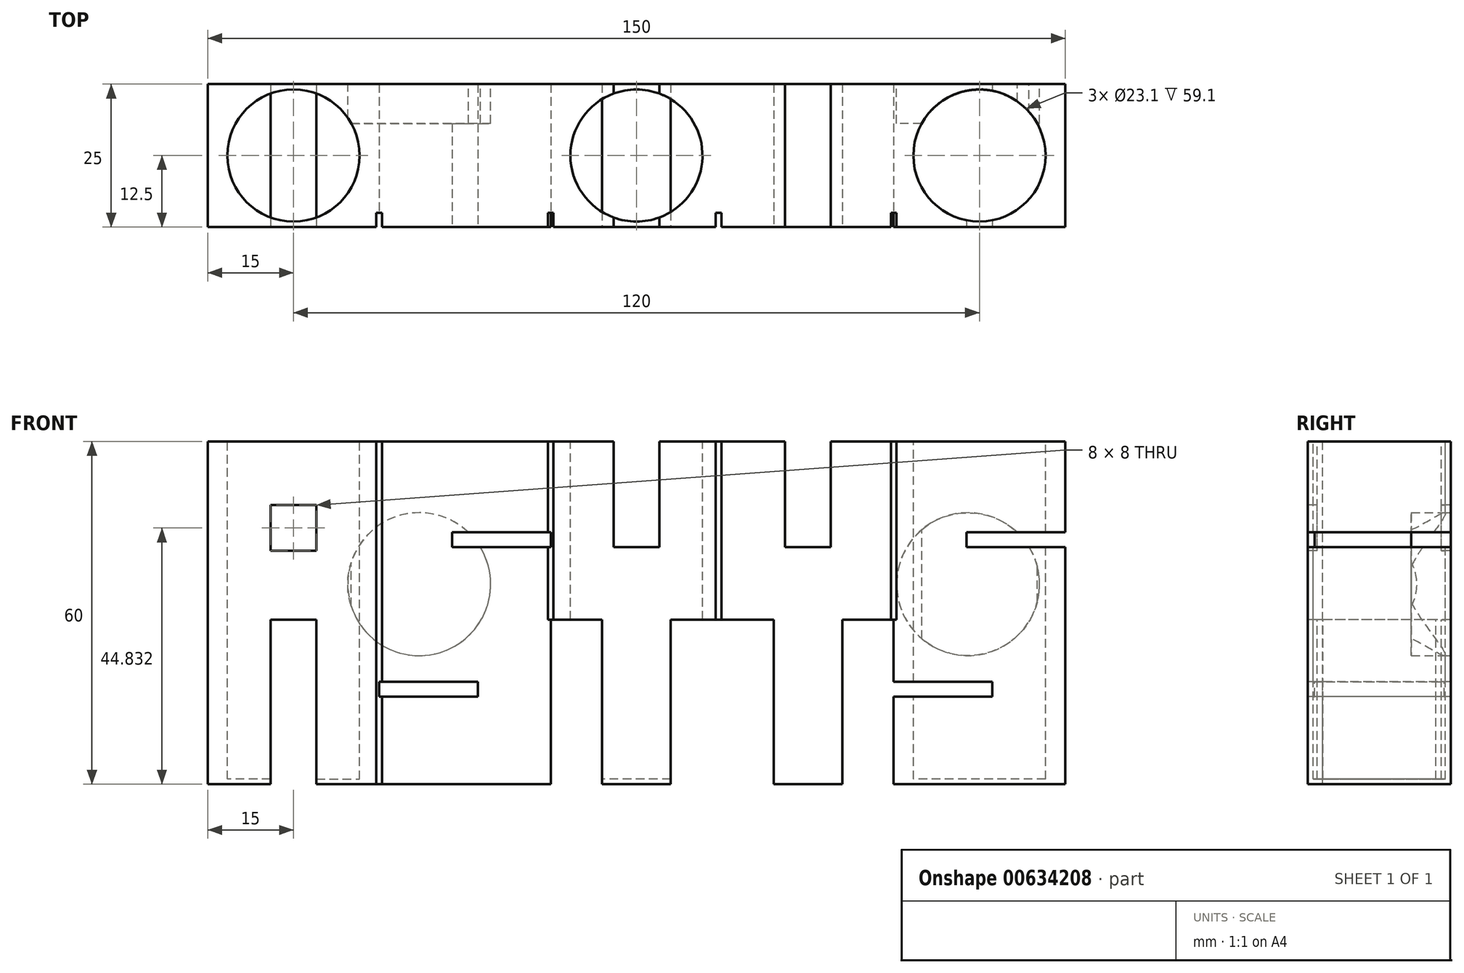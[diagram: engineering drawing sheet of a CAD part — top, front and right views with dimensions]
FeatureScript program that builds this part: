
annotation { "Feature Type Name" : "Feature", "Feature Type Description" : "" }
export const myFeature = defineFeature(function(context is Context, id is Id, definition is map)
    precondition{}
    {
        {
            var Q0;
            Q0=qCreatedBy(makeId("Front.planeOp"),FACE);
            var sketch = newSketch(context, id + "F0", { "sketchPlane" : qUnion([Q0])});
            skLineSegment(sketch, "E0.bottom", {"start": v(-75, 38.6) * mm, "end": v(75, 38.6) * mm});
            skLineSegment(sketch, "E0.top", {"start": v(-75, -21.4) * mm, "end": v(75, -21.4) * mm});
            skLineSegment(sketch, "E0.left", {"start": v(-75, 38.6) * mm, "end": v(-75, -21.4) * mm});
            skLineSegment(sketch, "E0.right", {"start": v(75, 38.6) * mm, "end": v(75, -21.4) * mm});
            skSolve(sketch);
        }
        {
            var Q0;
            Q0 = qSketchRegion(id + "F0", true);
            extrude(context, id + "F1", {"entities" : qUnion([Q0]), "depth" : 25 * mm, "offsetDistance" : 25 * mm});
        }
        {
            var Q0;
            Q0=makeQuery(id+"F1.opExtrude","SWEPT_FACE",FACE,{"disambiguationData":[OSD([sQuery(id+"F0.wireOp",EDGE,"E0.bottom")])]});
            var sketch = newSketch(context, id + "F2", { "sketchPlane" : qUnion([Q0])});
            skLineSegment(sketch, "E1.bottom", {"start": v(-73, -2) * mm, "end": v(73, -2) * mm});
            skLineSegment(sketch, "E1.top", {"start": v(-73, -23) * mm, "end": v(73, -23) * mm});
            skLineSegment(sketch, "E1.left", {"start": v(-73, -2) * mm, "end": v(-73, -23) * mm});
            skLineSegment(sketch, "E1.right", {"start": v(73, -2) * mm, "end": v(73, -23) * mm});
            skLineSegment(sketch, "E2.MirrorCS", {"start": v(219, -2) * mm, "end": v(219, -23) * mm});
            skSolve(sketch);
        }
        {
            var Q0;
            Q0 = qSketchRegion(id + "F2", true);
            extrude(context, id + "F3", {"entities" : qUnion([Q0]), "operationType" : NewBodyOperationType.ADD, "oppositeDirection" : true, "depth" : 2 * mm, "offsetDistance" : 25 * mm});
        }
        {
            var Q0;
            Q0=makeQuery(id+"F3.boolean.opBoolean","MERGE",FACE,{"derivedFrom":[makeQuery(id+"F1.opExtrude","SWEPT_FACE",FACE,{"disambiguationData":[OSD([sQuery(id+"F0.wireOp",EDGE,"E0.bottom")])]}),makeQuery(id+"F3.opExtrude","CAP_FACE",FACE,{"disambiguationData":[OSD([sQuery(id+"F2.wireOp",EDGE,"E1.bottom"),sQuery(id+"F2.wireOp",EDGE,"E1.top"),sQuery(id+"F2.wireOp",EDGE,"E1.left"),sQuery(id+"F2.wireOp",EDGE,"E1.right")])],"isStart":true})]});
            var sketch = newSketch(context, id + "F4", { "sketchPlane" : qUnion([Q0])});
            skCircle(sketch, "E3", {"center": v(60, -12.5) * mm, "radius": 11.55 * mm});
            skCircle(sketch, "E4.MirrorC", {"center": v(-60, -12.5) * mm, "radius": 11.55 * mm});
            skCircle(sketch, "E5", {"center": v(0, -12.5) * mm, "radius": 11.55 * mm});
            skSolve(sketch);
        }
        {
            var Q0;
            Q0 = qSketchRegion(id + "F4", true);
            extrude(context, id + "F5", {"entities" : qUnion([Q0]), "operationType" : NewBodyOperationType.REMOVE, "oppositeDirection" : true, "depth" : 59.1 * mm, "offsetDistance" : 25 * mm});
        }
        {
            var Q0;
            Q0=makeQuery(id+"F1.opExtrude","CAP_FACE",FACE,{"disambiguationData":[OSD([sQuery(id+"F0.wireOp",EDGE,"E0.bottom"),sQuery(id+"F0.wireOp",EDGE,"E0.top"),sQuery(id+"F0.wireOp",EDGE,"E0.left"),sQuery(id+"F0.wireOp",EDGE,"E0.right")])],"isStart":true});
            var sketch = newSketch(context, id + "F6", { "sketchPlane" : qUnion([Q0])});
            skCircle(sketch, "E6", {"center": v(-58, 13.6) * mm, "radius": 12.5 * mm});
            skCircle(sketch, "E7.MirrorC", {"center": v(38, 13.6) * mm, "radius": 12.5 * mm});
            skSolve(sketch);
        }
        {
            var Q0;
            Q0 = qSketchRegion(id + "F6", true);
            extrude(context, id + "F7", {"entities" : qUnion([Q0]), "operationType" : NewBodyOperationType.REMOVE, "oppositeDirection" : true, "depth" : 6.9 * mm, "offsetDistance" : 25 * mm});
        }
        {
            var Q0;
            Q0=makeQuery(id+"F1.opExtrude","CAP_FACE",FACE,{"disambiguationData":[OSD([sQuery(id+"F0.wireOp",EDGE,"E0.bottom"),sQuery(id+"F0.wireOp",EDGE,"E0.top"),sQuery(id+"F0.wireOp",EDGE,"E0.left"),sQuery(id+"F0.wireOp",EDGE,"E0.right")])],"isStart":false});
            var sketch = newSketch(context, id + "F8", { "sketchPlane" : qUnion([Q0])});
            skLineSegment(sketch, "E8.bottom", {"start": v(-75, 38.6) * mm, "end": v(-45, 38.6) * mm});
            skLineSegment(sketch, "E8.top", {"start": v(-75, -21.4) * mm, "end": v(-45, -21.4) * mm});
            skLineSegment(sketch, "E8.left", {"start": v(-75, 38.6) * mm, "end": v(-75, -21.4) * mm});
            skLineSegment(sketch, "E8.right", {"start": v(-45, 38.6) * mm, "end": v(-45, -21.4) * mm});
            skLineSegment(sketch, "E9", {"start": v(-60, 38.6) * mm, "end": v(-60, -21.4) * mm});
            skLineSegment(sketch, "E10", {"start": v(-64, -21.4) * mm, "end": v(-64, 7.4) * mm});
            skLineSegment(sketch, "E11", {"start": v(-64, 7.4) * mm, "end": v(-60, 7.4) * mm});
            skLineSegment(sketch, "E12", {"start": v(-60, 27.44) * mm, "end": v(-64, 27.44) * mm});
            skLineSegment(sketch, "E13", {"start": v(-64, 27.44) * mm, "end": v(-64, 19.44) * mm});
            skLineSegment(sketch, "E14", {"start": v(-64, 19.44) * mm, "end": v(-60, 19.44) * mm});
            skLineSegment(sketch, "E15.MirrorCS", {"start": v(-60, 27.44) * mm, "end": v(-56, 27.44) * mm});
            skLineSegment(sketch, "E16.MirrorCS", {"start": v(-56, 27.44) * mm, "end": v(-56, 19.44) * mm});
            skLineSegment(sketch, "E17.MirrorCS", {"start": v(-56, 19.44) * mm, "end": v(-60, 19.44) * mm});
            skLineSegment(sketch, "E18.MirrorCS", {"start": v(-56, 7.4) * mm, "end": v(-60, 7.4) * mm});
            skLineSegment(sketch, "E19.MirrorCS", {"start": v(-56, -21.4) * mm, "end": v(-56, 7.4) * mm});
            skLineSegment(sketch, "E20.bottom", {"start": v(-45, 38.6) * mm, "end": v(-15, 38.6) * mm});
            skLineSegment(sketch, "E20.top", {"start": v(-45, -21.4) * mm, "end": v(-15, -21.4) * mm});
            skLineSegment(sketch, "E20.right", {"start": v(-15, 38.6) * mm, "end": v(-15, -21.4) * mm});
            skLineSegment(sketch, "E21.bottom", {"start": v(-15, 20.1) * mm, "end": v(-32.25, 20.1) * mm});
            skLineSegment(sketch, "E21.top", {"start": v(-15, 22.68) * mm, "end": v(-32.25, 22.68) * mm});
            skLineSegment(sketch, "E21.left", {"start": v(-15, 22.68) * mm, "end": v(-15, 20.1) * mm});
            skLineSegment(sketch, "E21.right", {"start": v(-32.25, 22.68) * mm, "end": v(-32.25, 20.1) * mm});
            skLineSegment(sketch, "E22.bottom", {"start": v(-45, -3.49) * mm, "end": v(-27.75, -3.49) * mm});
            skLineSegment(sketch, "E22.top", {"start": v(-45, -6.06) * mm, "end": v(-27.75, -6.06) * mm});
            skLineSegment(sketch, "E22.left", {"start": v(-45, -3.49) * mm, "end": v(-45, -6.06) * mm});
            skLineSegment(sketch, "E22.right", {"start": v(-27.75, -3.49) * mm, "end": v(-27.75, -6.06) * mm});
            skLineSegment(sketch, "E23.bottom", {"start": v(-15, 38.6) * mm, "end": v(15, 38.6) * mm});
            skLineSegment(sketch, "E23.top", {"start": v(-15, -21.4) * mm, "end": v(15, -21.4) * mm});
            skLineSegment(sketch, "E23.right", {"start": v(15, 38.6) * mm, "end": v(15, -21.4) * mm});
            skLineSegment(sketch, "E24", {"start": v(-4, 38.6) * mm, "end": v(-4, 20.1) * mm});
            skLineSegment(sketch, "E25", {"start": v(-4, 20.1) * mm, "end": v(0, 20.1) * mm});
            skLineSegment(sketch, "E26.MirrorCS", {"start": v(4, 38.6) * mm, "end": v(4, 20.1) * mm});
            skLineSegment(sketch, "E27.MirrorCS", {"start": v(4, 20.1) * mm, "end": v(0, 20.1) * mm});
            skLineSegment(sketch, "E28", {"start": v(-15, 7.4) * mm, "end": v(-6, 7.4) * mm});
            skLineSegment(sketch, "E29", {"start": v(-6, 7.4) * mm, "end": v(-6, -21.4) * mm});
            skLineSegment(sketch, "E30.bottom", {"start": v(15, 38.6) * mm, "end": v(45, 38.6) * mm});
            skLineSegment(sketch, "E30.top", {"start": v(15, -21.4) * mm, "end": v(45, -21.4) * mm});
            skLineSegment(sketch, "E30.right", {"start": v(45, 38.6) * mm, "end": v(45, -21.4) * mm});
            skLineSegment(sketch, "E31", {"start": v(30, 38.6) * mm, "end": v(30, -21.4) * mm});
            skLineSegment(sketch, "E32", {"start": v(26, 20.1) * mm, "end": v(30, 20.1) * mm});
            skLineSegment(sketch, "E33", {"start": v(26, 20.1) * mm, "end": v(26, 38.6) * mm});
            skLineSegment(sketch, "E34.MirrorCS", {"start": v(34, 20.1) * mm, "end": v(34, 38.6) * mm});
            skLineSegment(sketch, "E35.MirrorCS", {"start": v(34, 20.1) * mm, "end": v(30, 20.1) * mm});
            skLineSegment(sketch, "E36", {"start": v(15, 7.4) * mm, "end": v(24, 7.4) * mm});
            skLineSegment(sketch, "E37", {"start": v(24, 7.4) * mm, "end": v(24, -21.4) * mm});
            skLineSegment(sketch, "E38.MirrorCS", {"start": v(45, 7.4) * mm, "end": v(36, 7.4) * mm});
            skLineSegment(sketch, "E39.MirrorCS", {"start": v(36, 7.4) * mm, "end": v(36, -21.4) * mm});
            skLineSegment(sketch, "E40.MirrorCS", {"start": v(6, 7.4) * mm, "end": v(6, -21.4) * mm});
            skLineSegment(sketch, "E41", {"start": v(6, 7.4) * mm, "end": v(15, 7.4) * mm});
            skLineSegment(sketch, "E42", {"start": v(57.75, 22.68) * mm, "end": v(75, 22.68) * mm});
            skLineSegment(sketch, "E43", {"start": v(57.75, 20.1) * mm, "end": v(75, 20.1) * mm});
            skPoint(sketch, "E43.startSnap0", {"position": v(32, 20.1) * mm});
            skLineSegment(sketch, "E44", {"start": v(57.75, 22.68) * mm, "end": v(57.75, 20.1) * mm});
            skLineSegment(sketch, "E45", {"start": v(45, -3.49) * mm, "end": v(62.25, -3.49) * mm});
            skLineSegment(sketch, "E46", {"start": v(62.25, -3.49) * mm, "end": v(62.25, -6.06) * mm});
            skLineSegment(sketch, "E47", {"start": v(62.25, -6.06) * mm, "end": v(45, -6.06) * mm});
            skSolve(sketch);
        }
        {
            var Q0;
            {var subQ0=sQuery(id+"F8.wireOp",EDGE,"E12");Q0=makeQuery(id+"F8.imprint","IMPRINT",FACE,{"disambiguationData":[TD([[makeQuery(id+"F8.imprint","IMPRINT",EDGE,{"derivedFrom":subQ0}),1.0]])]});}
            var Q1;
            {var subQ0=sQuery(id+"F8.wireOp",EDGE,"E15.MirrorCS");Q1=makeQuery(id+"F8.imprint","IMPRINT",FACE,{"disambiguationData":[TD([[makeQuery(id+"F8.imprint","IMPRINT",EDGE,{"derivedFrom":subQ0}),-1.0]])]});}
            var Q2;
            {var subQ3=sQuery(id+"F8.wireOp",EDGE,"E10");Q2=makeQuery(id+"F8.imprint","IMPRINT",FACE,{"disambiguationData":[TD([[makeQuery(id+"F8.imprint","IMPRINT",EDGE,{"derivedFrom":subQ3}),-1.0]])]});}
            var Q3;
            {var subQ4=sQuery(id+"F8.wireOp",EDGE,"E18.MirrorCS");Q3=makeQuery(id+"F8.imprint","IMPRINT",FACE,{"disambiguationData":[TD([[makeQuery(id+"F8.imprint","IMPRINT",EDGE,{"derivedFrom":subQ4}),1.0]])]});}
            var Q4;
            Q4=makeQuery(id+"F8.imprint","IMPRINT",FACE,{"disambiguationData":[TD([[makeQuery(id+"F8.imprint","IMPRINT",EDGE,{"derivedFrom":sQuery(id+"F8.wireOp",EDGE,"E22.bottom")}),-1.0]])]});
            var Q5;
            {var subQ0=sQuery(id+"F8.wireOp",EDGE,"E21.bottom");Q5=makeQuery(id+"F8.imprint","IMPRINT",FACE,{"disambiguationData":[TD([[makeQuery(id+"F8.imprint","IMPRINT",EDGE,{"derivedFrom":subQ0}),-1.0]])]});}
            var Q6;
            {var subQ1=sQuery(id+"F8.wireOp",EDGE,"E24");Q6=makeQuery(id+"F8.imprint","IMPRINT",FACE,{"disambiguationData":[TD([[makeQuery(id+"F8.imprint","IMPRINT",EDGE,{"derivedFrom":subQ1}),1.0]])]});}
            var Q7;
            {var subQ4=sQuery(id+"F8.wireOp",EDGE,"E28");Q7=makeQuery(id+"F8.imprint","IMPRINT",FACE,{"disambiguationData":[TD([[makeQuery(id+"F8.imprint","IMPRINT",EDGE,{"derivedFrom":subQ4}),-1.0]])]});}
            var Q8;
            {var subQ3=sQuery(id+"F8.wireOp",EDGE,"E40.MirrorCS");Q8=makeQuery(id+"F8.imprint","IMPRINT",FACE,{"disambiguationData":[TD([[makeQuery(id+"F8.imprint","IMPRINT",EDGE,{"derivedFrom":subQ3}),1.0]])]});}
            var Q9;
            {var subQ4=sQuery(id+"F8.wireOp",EDGE,"E36");Q9=makeQuery(id+"F8.imprint","IMPRINT",FACE,{"disambiguationData":[TD([[makeQuery(id+"F8.imprint","IMPRINT",EDGE,{"derivedFrom":subQ4}),-1.0]])]});}
            var Q10;
            {var subQ3=sQuery(id+"F8.wireOp",EDGE,"E34.MirrorCS");Q10=makeQuery(id+"F8.imprint","IMPRINT",FACE,{"disambiguationData":[TD([[makeQuery(id+"F8.imprint","IMPRINT",EDGE,{"derivedFrom":subQ3}),1.0]])]});}
            var Q11;
            {var subQ4=sQuery(id+"F8.wireOp",EDGE,"E32");Q11=makeQuery(id+"F8.imprint","IMPRINT",FACE,{"disambiguationData":[TD([[makeQuery(id+"F8.imprint","IMPRINT",EDGE,{"derivedFrom":subQ4}),1.0]])]});}
            var Q12;
            {var subQ4=sQuery(id+"F8.wireOp",EDGE,"E38.MirrorCS");Q12=makeQuery(id+"F8.imprint","IMPRINT",FACE,{"disambiguationData":[TD([[makeQuery(id+"F8.imprint","IMPRINT",EDGE,{"derivedFrom":subQ4}),1.0]])]});}
            var Q13;
            {var subQ0=sQuery(id+"F8.wireOp",EDGE,"E45");Q13=makeQuery(id+"F8.imprint","IMPRINT",FACE,{"disambiguationData":[TD([[makeQuery(id+"F8.imprint","IMPRINT",EDGE,{"derivedFrom":subQ0}),-1.0]])]});}
            var Q14;
            {var subQ0=sQuery(id+"F8.wireOp",EDGE,"E42");Q14=makeQuery(id+"F8.imprint","IMPRINT",FACE,{"disambiguationData":[TD([[makeQuery(id+"F8.imprint","IMPRINT",EDGE,{"derivedFrom":subQ0}),-1.0]])]});}
            extrude(context, id + "F9", {"entities" : qUnion([Q0, Q1, Q2, Q3, Q4, Q5, Q6, Q7, Q8, Q9, Q10, Q11, Q12, Q13, Q14]), "operationType" : NewBodyOperationType.REMOVE, "oppositeDirection" : true, "depth" : 35.6 * mm, "offsetDistance" : 25 * mm});
        }
        {
            var Q0;
            Q0=makeQuery(id+"F1.opExtrude","CAP_FACE",FACE,{"disambiguationData":[OSD([sQuery(id+"F0.wireOp",EDGE,"E0.bottom"),sQuery(id+"F0.wireOp",EDGE,"E0.top"),sQuery(id+"F0.wireOp",EDGE,"E0.left"),sQuery(id+"F0.wireOp",EDGE,"E0.right")])],"isStart":false});
            var sketch = newSketch(context, id + "F10", { "sketchPlane" : qUnion([Q0])});
            skPoint(sketch, "E48.oppositeSnap0", {"position": v(-45, -4.78) * mm});
            skLineSegment(sketch, "E48.bottom", {"start": v(-75, 38.6) * mm, "end": v(-45, 38.6) * mm});
            skLineSegment(sketch, "E48.top", {"start": v(-75, -21.4) * mm, "end": v(-45, -21.4) * mm});
            skLineSegment(sketch, "E48.left", {"start": v(-75, 38.6) * mm, "end": v(-75, -21.4) * mm});
            skLineSegment(sketch, "E48.right", {"start": v(-45, 38.6) * mm, "end": v(-45, -21.4) * mm});
            skLineSegment(sketch, "E49.bottom", {"start": v(-45, 38.6) * mm, "end": v(-15, 38.6) * mm});
            skLineSegment(sketch, "E49.top", {"start": v(-45, -21.4) * mm, "end": v(-15, -21.4) * mm});
            skLineSegment(sketch, "E49.right", {"start": v(-15, 38.6) * mm, "end": v(-15, -21.4) * mm});
            skLineSegment(sketch, "E50.bottom", {"start": v(-15, 38.6) * mm, "end": v(14.35, 38.6) * mm});
            skLineSegment(sketch, "E50.top", {"start": v(-15, -21.4) * mm, "end": v(14.35, -21.4) * mm});
            skLineSegment(sketch, "E50.right", {"start": v(14.35, 38.6) * mm, "end": v(14.35, -21.4) * mm});
            skLineSegment(sketch, "E51.bottom", {"start": v(14.35, 38.6) * mm, "end": v(45, 38.6) * mm});
            skLineSegment(sketch, "E51.top", {"start": v(14.35, -21.4) * mm, "end": v(45, -21.4) * mm});
            skLineSegment(sketch, "E51.right", {"start": v(45, 38.6) * mm, "end": v(45, -21.4) * mm});
            skLineSegment(sketch, "E52", {"start": v(-45.5, 38.6) * mm, "end": v(-45.5, -21.4) * mm});
            skLineSegment(sketch, "E53.MirrorCS", {"start": v(-44.5, 38.6) * mm, "end": v(-44.5, -21.4) * mm});
            skLineSegment(sketch, "E54", {"start": v(-14.5, 38.6) * mm, "end": v(-14.5, 7.4) * mm});
            skLineSegment(sketch, "E55", {"start": v(13.85, 38.6) * mm, "end": v(13.85, 7.4) * mm});
            skLineSegment(sketch, "E56.MirrorCS", {"start": v(14.85, 38.6) * mm, "end": v(14.85, 7.4) * mm});
            skLineSegment(sketch, "E57", {"start": v(44.5, 38.6) * mm, "end": v(44.5, 7.4) * mm});
            skLineSegment(sketch, "E58.MirrorCS", {"start": v(-15.5, 38.6) * mm, "end": v(-15.5, 7.4) * mm});
            skLineSegment(sketch, "E59", {"start": v(-15.5, 7.4) * mm, "end": v(-15, 7.4) * mm});
            skLineSegment(sketch, "E60.MirrorCS", {"start": v(45.5, 38.6) * mm, "end": v(45.5, 7.4) * mm});
            skLineSegment(sketch, "E61", {"start": v(45, 7.4) * mm, "end": v(45.5, 7.4) * mm});
            skSolve(sketch);
        }
        {
            var Q0;
            {var subQ1=makeQuery(id+"F9.boolean.opBoolean","COPY",EDGE,{"derivedFrom":makeQuery(id+"F9.opExtrude","CAP_EDGE",EDGE,{"disambiguationData":[OSD([sQuery(id+"F8.wireOp",EDGE,"E10")])],"isStart":true})});Q0=makeQuery(id+"F10.imprint","IMPRINT",FACE,{"disambiguationData":[TD([[makeQuery(id+"F10.imprint","IMPRINT",EDGE,{"derivedFrom":subQ1}),-1.0]])]});}
            var Q1;
            {var subQ1=makeQuery(id+"F9.boolean.opBoolean","COPY",EDGE,{"derivedFrom":makeQuery(id+"F9.opExtrude","CAP_EDGE",EDGE,{"disambiguationData":[OSD([sQuery(id+"F8.wireOp",EDGE,"E24")])],"isStart":true})});Q1=makeQuery(id+"F10.imprint","IMPRINT",FACE,{"disambiguationData":[TD([[makeQuery(id+"F10.imprint","IMPRINT",EDGE,{"derivedFrom":subQ1}),1.0]])]});}
            var Q2;
            {var subQ1=makeQuery(id+"F9.boolean.opBoolean","COPY",EDGE,{"derivedFrom":makeQuery(id+"F9.opExtrude","CAP_EDGE",EDGE,{"disambiguationData":[OSD([sQuery(id+"F8.wireOp",EDGE,"E33")])],"isStart":true})});Q2=makeQuery(id+"F10.imprint","IMPRINT",FACE,{"disambiguationData":[TD([[makeQuery(id+"F10.imprint","IMPRINT",EDGE,{"derivedFrom":subQ1}),-1.0]])]});}
            var Q3;
            Q3=makeQuery(id+"F10.imprint","IMPRINT",FACE,{"disambiguationData":[TD([[makeQuery(id+"F10.imprint","IMPRINT",EDGE,{"derivedFrom":makeQuery(id+"F9.boolean.opBoolean","COPY",EDGE,{"derivedFrom":makeQuery(id+"F9.opExtrude","CAP_EDGE",EDGE,{"disambiguationData":[OSD([sQuery(id+"F8.wireOp",EDGE,"E13")])],"isStart":true})})}),1.0]])]});
            var Q4;
            {var subQ1=sQuery(id+"F10.wireOp",EDGE,"E49.top");var subQ3=sQuery(id+"F10.wireOp",EDGE,"E53.MirrorCS");var subQ4=makeQuery(id+"F10.imprint","INTERSECT",VERTEX,{"derivedFrom":[subQ1,subQ3]});Q4=makeQuery(id+"F10.imprint","IMPRINT",FACE,{"disambiguationData":[TD([[makeQuery(id+"F10.imprint","IMPRINT",EDGE,{"disambiguationData":[TD([[subQ4,1.0]])],"derivedFrom":subQ3}),-1.0]])]});}
            var Q5;
            {var subQ5=makeQuery(id+"F9.boolean.opBoolean","COPY",EDGE,{"derivedFrom":makeQuery(id+"F9.opExtrude","CAP_EDGE",EDGE,{"disambiguationData":[OSD([sQuery(id+"F8.wireOp",EDGE,"E22.right")])],"isStart":true})});Q5=makeQuery(id+"F10.imprint","IMPRINT",FACE,{"disambiguationData":[TD([[makeQuery(id+"F10.imprint","IMPRINT",EDGE,{"derivedFrom":subQ5}),-1.0]])]});}
            var Q6;
            {var subQ5=makeQuery(id+"F9.boolean.opBoolean","COPY",EDGE,{"derivedFrom":makeQuery(id+"F9.opExtrude","CAP_EDGE",EDGE,{"disambiguationData":[OSD([sQuery(id+"F8.wireOp",EDGE,"E21.right")])],"isStart":true})});Q6=makeQuery(id+"F10.imprint","IMPRINT",FACE,{"disambiguationData":[TD([[makeQuery(id+"F10.imprint","IMPRINT",EDGE,{"derivedFrom":subQ5}),1.0]])]});}
            var Q7;
            {var subQ0=makeQuery(id+"F9.boolean.opBoolean","COPY",EDGE,{"derivedFrom":makeQuery(id+"F9.opExtrude","CAP_EDGE",EDGE,{"disambiguationData":[OSD([sQuery(id+"F8.wireOp",EDGE,"E29")])],"isStart":true})});Q7=makeQuery(id+"F10.imprint","IMPRINT",FACE,{"disambiguationData":[TD([[makeQuery(id+"F10.imprint","IMPRINT",EDGE,{"derivedFrom":subQ0}),-1.0]])]});}
            var Q8;
            {var subQ0=makeQuery(id+"F9.boolean.opBoolean","COPY",EDGE,{"derivedFrom":makeQuery(id+"F9.opExtrude","CAP_EDGE",EDGE,{"disambiguationData":[OSD([sQuery(id+"F8.wireOp",EDGE,"E40.MirrorCS")])],"isStart":true})});Q8=makeQuery(id+"F10.imprint","IMPRINT",FACE,{"disambiguationData":[TD([[makeQuery(id+"F10.imprint","IMPRINT",EDGE,{"derivedFrom":subQ0}),1.0]])]});}
            var Q9;
            {var subQ0=makeQuery(id+"F9.boolean.opBoolean","COPY",EDGE,{"derivedFrom":makeQuery(id+"F9.opExtrude","CAP_EDGE",EDGE,{"disambiguationData":[OSD([sQuery(id+"F8.wireOp",EDGE,"E37")])],"isStart":true})});Q9=makeQuery(id+"F10.imprint","IMPRINT",FACE,{"disambiguationData":[TD([[makeQuery(id+"F10.imprint","IMPRINT",EDGE,{"derivedFrom":subQ0}),-1.0]])]});}
            var Q10;
            {var subQ0=sQuery(id+"F10.wireOp",EDGE,"E48.right");var subQ1=makeQuery(id+"F9.boolean.opBoolean","COPY",EDGE,{"derivedFrom":makeQuery(id+"F9.opExtrude","CAP_EDGE",EDGE,{"disambiguationData":[OSD([sQuery(id+"F8.wireOp",EDGE,"E22.bottom")])],"isStart":true})});var subQ2=makeQuery(id+"F10.imprint","INTERSECT",VERTEX,{"derivedFrom":[subQ1,subQ0]});Q10=makeQuery(id+"F10.imprint","IMPRINT",FACE,{"disambiguationData":[TD([[makeQuery(id+"F10.imprint","IMPRINT",EDGE,{"disambiguationData":[TD([[subQ2,-1.0]])],"derivedFrom":subQ0}),1.0]])]});}
            var Q11;
            {var subQ10=makeQuery(id+"F9.boolean.opBoolean","COPY",EDGE,{"derivedFrom":makeQuery(id+"F9.opExtrude","CAP_EDGE",EDGE,{"disambiguationData":[OSD([sQuery(id+"F8.wireOp",EDGE,"E39.MirrorCS")])],"isStart":true})});Q11=makeQuery(id+"F10.imprint","IMPRINT",FACE,{"disambiguationData":[TD([[makeQuery(id+"F10.imprint","IMPRINT",EDGE,{"derivedFrom":subQ10}),1.0]])]});}
            var Q12;
            {var subQ6=sQuery(id+"F10.wireOp",EDGE,"E60.MirrorCS");Q12=makeQuery(id+"F10.imprint","IMPRINT",FACE,{"disambiguationData":[TD([[makeQuery(id+"F10.imprint","IMPRINT",EDGE,{"derivedFrom":subQ6}),-1.0]])]});}
            var Q13;
            {var subQ5=sQuery(id+"F10.wireOp",EDGE,"E57");Q13=makeQuery(id+"F10.imprint","IMPRINT",FACE,{"disambiguationData":[TD([[makeQuery(id+"F10.imprint","IMPRINT",EDGE,{"derivedFrom":subQ5}),1.0]])]});}
            var Q14;
            {var subQ3=sQuery(id+"F10.wireOp",EDGE,"E56.MirrorCS");Q14=makeQuery(id+"F10.imprint","IMPRINT",FACE,{"disambiguationData":[TD([[makeQuery(id+"F10.imprint","IMPRINT",EDGE,{"derivedFrom":subQ3}),-1.0]])]});}
            var Q15;
            {var subQ3=sQuery(id+"F10.wireOp",EDGE,"E55");Q15=makeQuery(id+"F10.imprint","IMPRINT",FACE,{"disambiguationData":[TD([[makeQuery(id+"F10.imprint","IMPRINT",EDGE,{"derivedFrom":subQ3}),1.0]])]});}
            var Q16;
            {var subQ5=sQuery(id+"F10.wireOp",EDGE,"E54");Q16=makeQuery(id+"F10.imprint","IMPRINT",FACE,{"disambiguationData":[TD([[makeQuery(id+"F10.imprint","IMPRINT",EDGE,{"derivedFrom":subQ5}),-1.0]])]});}
            var Q17;
            {var subQ1=sQuery(id+"F10.wireOp",EDGE,"E49.bottom");var subQ3=sQuery(id+"F10.wireOp",EDGE,"E58.MirrorCS");var subQ4=makeQuery(id+"F10.imprint","INTERSECT",VERTEX,{"derivedFrom":[subQ1,subQ3]});Q17=makeQuery(id+"F10.imprint","IMPRINT",FACE,{"disambiguationData":[TD([[makeQuery(id+"F10.imprint","IMPRINT",EDGE,{"disambiguationData":[TD([[subQ4,-1.0]])],"derivedFrom":subQ3}),1.0]])]});}
            var Q18;
            {var subQ3=sQuery(id+"F10.wireOp",EDGE,"E59");Q18=makeQuery(id+"F10.imprint","IMPRINT",FACE,{"disambiguationData":[TD([[makeQuery(id+"F10.imprint","IMPRINT",EDGE,{"derivedFrom":subQ3}),1.0]])]});}
            var Q19;
            {var subQ0=sQuery(id+"F10.wireOp",EDGE,"E49.right");var subQ1=makeQuery(id+"F9.boolean.opBoolean","COPY",EDGE,{"derivedFrom":makeQuery(id+"F9.opExtrude","CAP_EDGE",EDGE,{"disambiguationData":[OSD([sQuery(id+"F8.wireOp",EDGE,"E21.bottom")])],"isStart":true})});var subQ2=makeQuery(id+"F10.imprint","INTERSECT",VERTEX,{"derivedFrom":[subQ1,subQ0]});Q19=makeQuery(id+"F10.imprint","IMPRINT",FACE,{"disambiguationData":[TD([[makeQuery(id+"F10.imprint","IMPRINT",EDGE,{"disambiguationData":[TD([[subQ2,1.0]])],"derivedFrom":subQ0}),-1.0]])]});}
            var Q20;
            {var subQ1=sQuery(id+"F10.wireOp",EDGE,"E49.bottom");var subQ3=sQuery(id+"F10.wireOp",EDGE,"E53.MirrorCS");var subQ4=makeQuery(id+"F10.imprint","INTERSECT",VERTEX,{"derivedFrom":[subQ1,subQ3]});Q20=makeQuery(id+"F10.imprint","IMPRINT",FACE,{"disambiguationData":[TD([[makeQuery(id+"F10.imprint","IMPRINT",EDGE,{"disambiguationData":[TD([[subQ4,-1.0]])],"derivedFrom":subQ3}),-1.0]])]});}
            var Q21;
            {var subQ5=sQuery(id+"F10.wireOp",EDGE,"E52");Q21=makeQuery(id+"F10.imprint","IMPRINT",FACE,{"disambiguationData":[TD([[makeQuery(id+"F10.imprint","IMPRINT",EDGE,{"derivedFrom":subQ5}),1.0]])]});}
            extrude(context, id + "F11", {"entities" : qUnion([Q0, Q1, Q2, Q3, Q4, Q5, Q6, Q7, Q8, Q9, Q10, Q11, Q12, Q13, Q14, Q15, Q16, Q17, Q18, Q19, Q20, Q21]), "operationType" : NewBodyOperationType.REMOVE, "oppositeDirection" : true, "depth" : 2.5 * mm, "offsetDistance" : 25 * mm});
        }
    });
